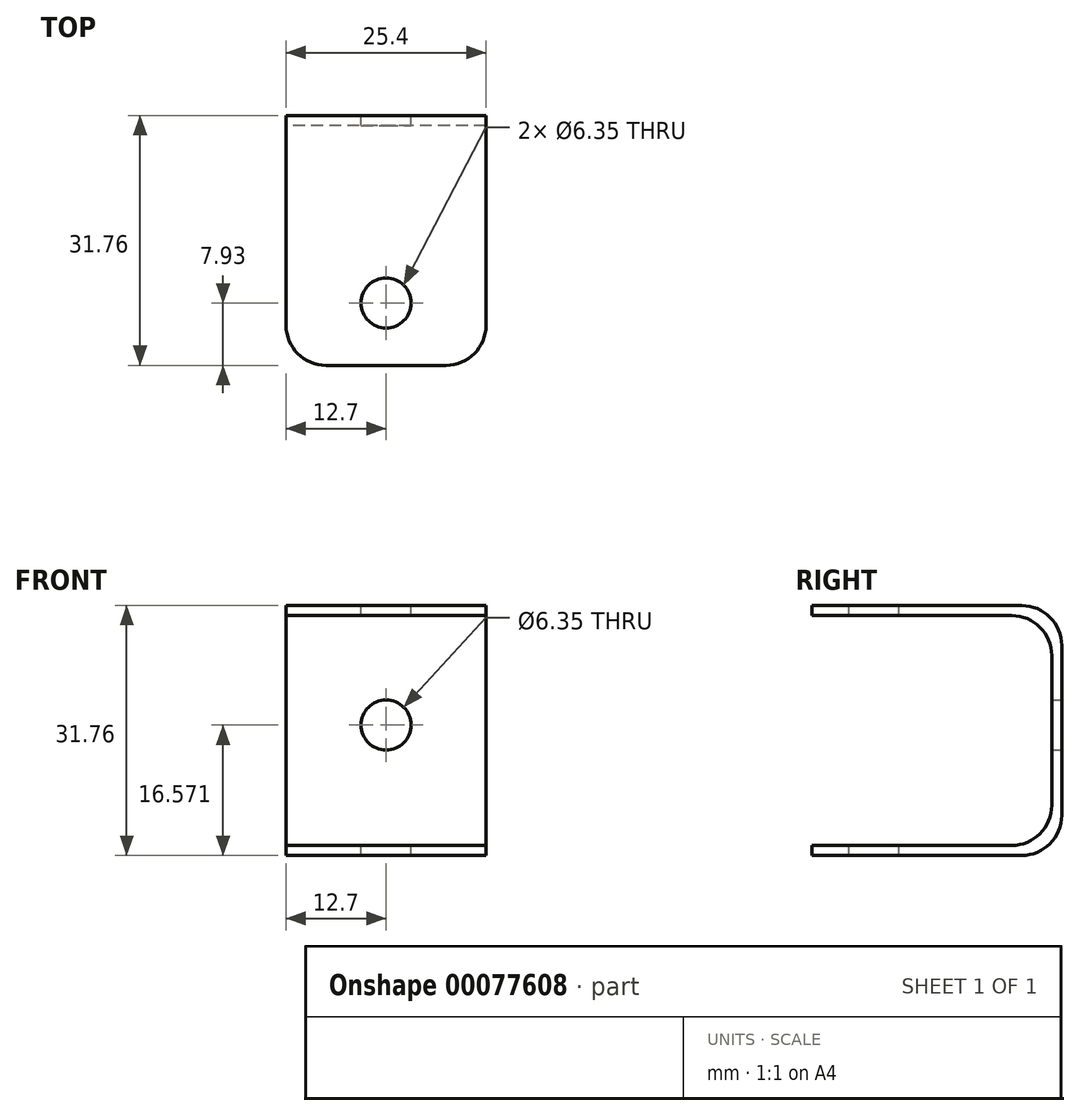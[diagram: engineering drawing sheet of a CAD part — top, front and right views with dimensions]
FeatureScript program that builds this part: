
annotation { "Feature Type Name" : "Feature", "Feature Type Description" : "" }
export const myFeature = defineFeature(function(context is Context, id is Id, definition is map)
    precondition{}
    {
        {
            var Q0;
            Q0=qCreatedBy(makeId("Right.planeOp"),FACE);
            var sketch = newSketch(context, id + "F0", { "sketchPlane" : qUnion([Q0])});
            skLineSegment(sketch, "E0.bottom", {"start": v(-15.88, 15.88) * mm, "end": v(15.88, 15.88) * mm});
            skLineSegment(sketch, "E0.top", {"start": v(-15.88, -15.88) * mm, "end": v(15.88, -15.88) * mm});
            skLineSegment(sketch, "E0.left", {"start": v(-15.88, 15.88) * mm, "end": v(-15.88, 14.6) * mm});
            skLineSegment(sketch, "E0.right", {"start": v(15.88, 15.88) * mm, "end": v(15.88, -15.88) * mm});
            skLineSegment(sketch, "E1.0", {"start": v(14.6, 14.6) * mm, "end": v(14.6, -14.6) * mm});
            skLineSegment(sketch, "E1.1", {"start": v(-14.6, 14.6) * mm, "end": v(14.6, 14.6) * mm});
            skLineSegment(sketch, "E1.3", {"start": v(-14.6, -14.6) * mm, "end": v(14.6, -14.6) * mm});
            skLineSegment(sketch, "E2", {"start": v(-14.6, 14.6) * mm, "end": v(-15.88, 14.6) * mm});
            skLineSegment(sketch, "E3", {"start": v(-14.6, -14.6) * mm, "end": v(-15.88, -14.6) * mm});
            skLineSegment(sketch, "E4.trimOffspring", {"start": v(-15.88, -14.6) * mm, "end": v(-15.88, -15.88) * mm});
            skSolve(sketch);
        }
        {
            var Q0;
            Q0 = qSketchRegion(id + "F0", true);
            extrude(context, id + "F1", {"entities" : qUnion([Q0]), "depth" : 12.7 * mm, "hasSecondDirection" : true, "secondDirectionOppositeDirection" : true, "secondDirectionDepth" : 12.7 * mm});
        }
        {
            var Q0;
            Q0=makeQuery(id+"F1.opExtrude","SWEPT_FACE",FACE,{"disambiguationData":[OSD([sQuery(id+"F0.wireOp",EDGE,"E0.bottom")])]});
            var sketch = newSketch(context, id + "F2", { "sketchPlane" : qUnion([Q0])});
            skCircle(sketch, "E5", {"center": v(0, -7.95) * mm, "radius": 3.18 * mm});
            skPoint(sketch, "E5.centerSnap0", {"position": v(0, -15.88) * mm});
            skSolve(sketch);
        }
        {
            var Q0;
            Q0 = qSketchRegion(id + "F2", true);
            extrude(context, id + "F3", {"entities" : qUnion([Q0]), "operationType" : NewBodyOperationType.REMOVE, "endBound" : BoundingType.THROUGH_ALL, "oppositeDirection" : true, "depth" : 25.4 * mm});
        }
        {
            var Q0;
            Q0=makeQuery(id+"F1.opExtrude","SWEPT_EDGE",EDGE,{"disambiguationData":[OSD([sQuery(id+"F0.wireOp",EDGE,"E0.bottom"),sQuery(id+"F0.wireOp",EDGE,"E0.right")])]});
            var Q1;
            Q1=makeQuery(id+"F1.opExtrude","SWEPT_EDGE",EDGE,{"disambiguationData":[OSD([sQuery(id+"F0.wireOp",EDGE,"E0.top"),sQuery(id+"F0.wireOp",EDGE,"E0.right")])]});
            var Q2;
            Q2=makeQuery(id+"F1.opExtrude","SWEPT_EDGE",EDGE,{"disambiguationData":[OSD([sQuery(id+"F0.wireOp",EDGE,"E1.0"),sQuery(id+"F0.wireOp",EDGE,"E1.1")])]});
            var Q3;
            Q3=makeQuery(id+"F1.opExtrude","SWEPT_EDGE",EDGE,{"disambiguationData":[OSD([sQuery(id+"F0.wireOp",EDGE,"E1.0"),sQuery(id+"F0.wireOp",EDGE,"E1.3")])]});
            fillet(context, id + "F4", {"entities" : qUnion([Q0, Q1, Q2, Q3]), "radius" : 5.08 * mm, "tangentPropagation" : true, "allowEdgeOverflow" : false});
        }
        {
            var Q0;
            Q0=makeQuery(id+"F1.opExtrude","CAP_EDGE",EDGE,{"disambiguationData":[OSD([sQuery(id+"F0.wireOp",EDGE,"E0.left")])],"isStart":false});
            var Q1;
            Q1=makeQuery(id+"F1.opExtrude","CAP_EDGE",EDGE,{"disambiguationData":[OSD([sQuery(id+"F0.wireOp",EDGE,"E0.left")])],"isStart":true});
            var Q2;
            Q2=makeQuery(id+"F1.opExtrude","CAP_EDGE",EDGE,{"disambiguationData":[OSD([sQuery(id+"F0.wireOp",EDGE,"E4.trimOffspring")])],"isStart":false});
            var Q3;
            Q3=makeQuery(id+"F1.opExtrude","CAP_EDGE",EDGE,{"disambiguationData":[OSD([sQuery(id+"F0.wireOp",EDGE,"E4.trimOffspring")])],"isStart":true});
            fillet(context, id + "F5", {"entities" : qUnion([Q0, Q1, Q2, Q3]), "radius" : 5.08 * mm, "tangentPropagation" : true, "allowEdgeOverflow" : false});
        }
        {
            var Q0;
            Q0=makeQuery(id+"F1.opExtrude","SWEPT_FACE",FACE,{"disambiguationData":[OSD([sQuery(id+"F0.wireOp",EDGE,"E0.right")])]});
            var sketch = newSketch(context, id + "F6", { "sketchPlane" : qUnion([Q0])});
            skCircle(sketch, "E6", {"center": v(0, 0.7) * mm, "radius": 3.18 * mm});
            skSolve(sketch);
        }
        {
            var Q0;
            Q0 = qSketchRegion(id + "F6", true);
            extrude(context, id + "F7", {"entities" : qUnion([Q0]), "operationType" : NewBodyOperationType.REMOVE, "endBound" : BoundingType.THROUGH_ALL, "oppositeDirection" : true, "depth" : 25.4 * mm});
        }
    });
